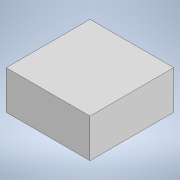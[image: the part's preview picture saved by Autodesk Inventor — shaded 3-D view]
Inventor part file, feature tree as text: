
AUTODESK INVENTOR PART (.ipt)
format: ipt  version: 2022 (Build 260153000, 153)  size: 103,424 bytes
history: native  units: in
note: dims shown in document units (in); Inventor stores cm internally (conversion verified against a paired STEP export)
features: extrude x2, sketch x2
ambient origin geometry x8: Origin, YZ Plane, XZ Plane, XY Plane, X Axis, Y Axis, Z Axis, Center Point
bodies: Solid1 (feature_tree)
feature tree (4):
  extrude  "Extrusion1"  Depth=0.2165in
  extrude  "Extrusion2"  Depth=0.2559in
  sketch  "Sketch2"  dims[d2=0.2165in d3=0.2165in]
  sketch  "Sketch4"  dims[d6=0.2559in d7=0.2559in d8=0.0787in d9=0.0in d10=0.2559in d11=0.0394in d12=0.0in]
